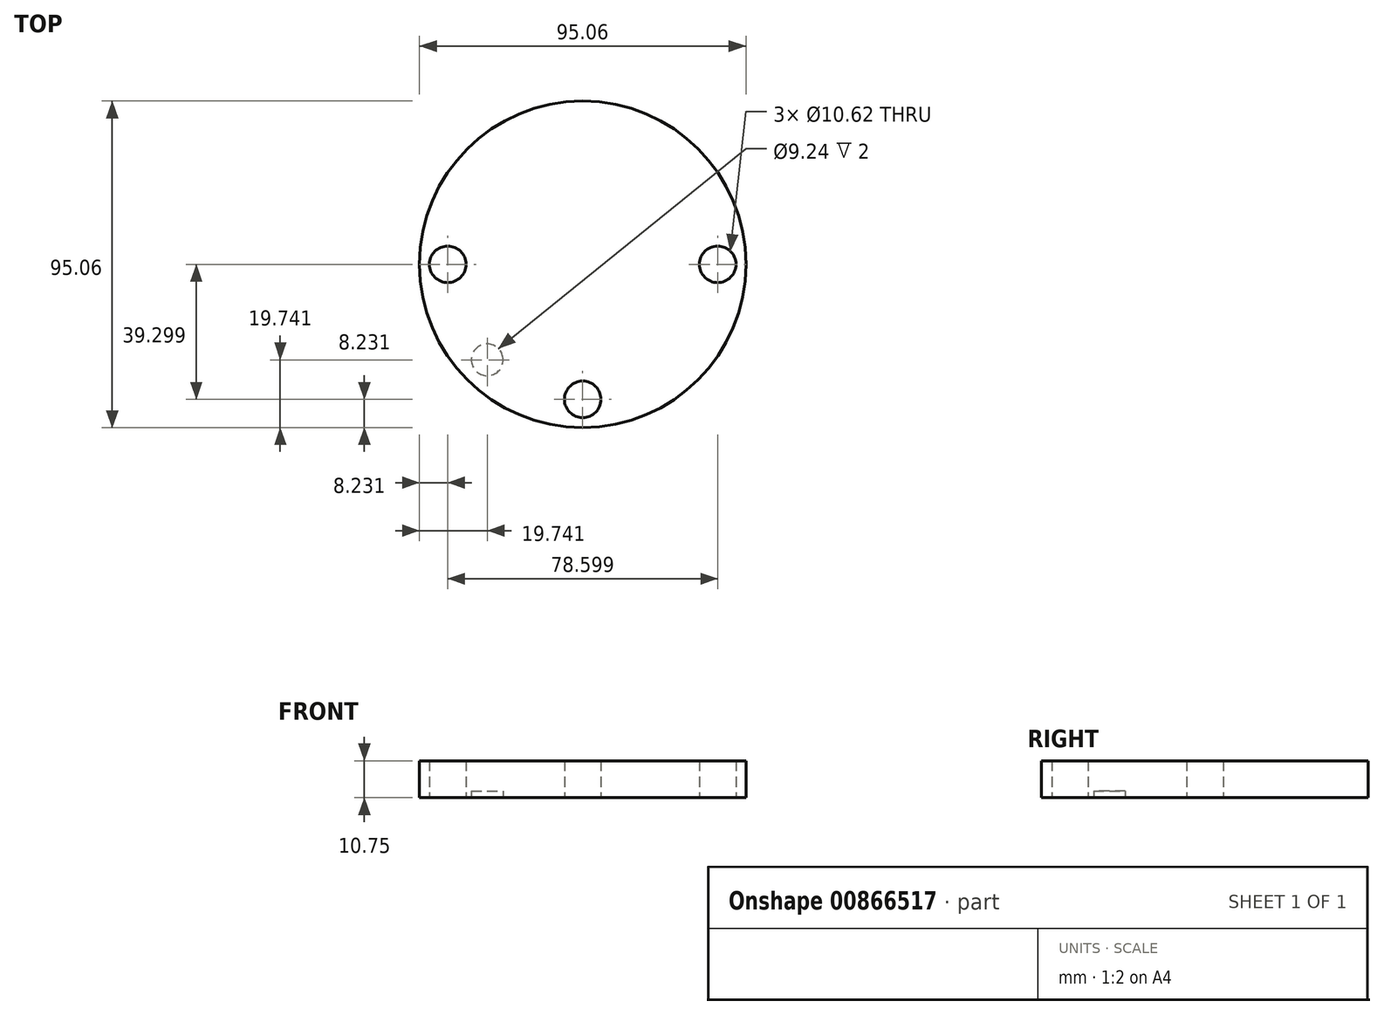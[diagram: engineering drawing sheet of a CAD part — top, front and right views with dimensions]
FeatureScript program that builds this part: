
annotation { "Feature Type Name" : "Feature", "Feature Type Description" : "" }
export const myFeature = defineFeature(function(context is Context, id is Id, definition is map)
    precondition{}
    {
        {
            var Q0;
            Q0=qCreatedBy(makeId("Front.planeOp"),FACE);
            var sketch = newSketch(context, id + "F0", { "sketchPlane" : qUnion([Q0])});
            skLineSegment(sketch, "E0", {"start": v(0, -21.77) * mm, "end": v(0, 44.18) * mm, "construction": true});
            skLineSegment(sketch, "E1", {"start": v(0, 0) * mm, "end": v(-47.53, 0) * mm});
            skLineSegment(sketch, "E2", {"start": v(-47.53, 0) * mm, "end": v(-47.53, -10.75) * mm});
            skLineSegment(sketch, "E3", {"start": v(-47.53, -10.75) * mm, "end": v(0, -10.75) * mm});
            skLineSegment(sketch, "E4", {"start": v(0, -10.75) * mm, "end": v(0, 0) * mm});
            skSolve(sketch);
        }
        {
            var Q0;
            Q0 = qSketchRegion(id + "F0", true);
            var Q1;
            Q1=sQuery(id+"F0.wireOp",EDGE,"E0");
            revolve(context, id + "F1", {"surfaceOperationType" : NewSurfaceOperationType.NEW, "entities" : qUnion([Q0]), "axis" : qUnion([Q1]), "revolveType" : RevolveType.FULL});
        }
        {
            var Q0;
            Q0=makeQuery(id+"F1.opRevolve","SWEPT_FACE",FACE,{"disambiguationData":[OSD([sQuery(id+"F0.wireOp",EDGE,"E3")])]});
            var sketch = newSketch(context, id + "F2", { "sketchPlane" : qUnion([Q0])});
            skLineSegment(sketch, "E5", {"start": v(0, 0) * mm, "end": v(0, 39.3) * mm, "construction": true});
            skLineSegment(sketch, "E6", {"start": v(0, 0) * mm, "end": v(-39.3, 0) * mm, "construction": true});
            skLineSegment(sketch, "E7", {"start": v(0, 0) * mm, "end": v(-27.79, 27.79) * mm, "construction": true});
            skCircle(sketch, "E8", {"center": v(0, 0) * mm, "radius": 39.3 * mm, "construction": true});
            skCircle(sketch, "E9", {"center": v(0, 39.3) * mm, "radius": 5.31 * mm});
            skCircle(sketch, "E10", {"center": v(-27.79, 27.79) * mm, "radius": 4.62 * mm});
            skCircle(sketch, "E11", {"center": v(-39.3, 0) * mm, "radius": 5.31 * mm});
            skCircle(sketch, "E12", {"center": v(39.3, 0) * mm, "radius": 5.31 * mm});
            skSolve(sketch);
        }
        {
            var Q0;
            Q0=makeQuery(id+"F2.imprint","IMPRINT",FACE,{"disambiguationData":[TD([[makeQuery(id+"F2.imprint","IMPRINT",EDGE,{"derivedFrom":sQuery(id+"F2.wireOp",EDGE,"E11")}),1.0]])]});
            var Q1;
            Q1=makeQuery(id+"F2.imprint","IMPRINT",FACE,{"disambiguationData":[TD([[makeQuery(id+"F2.imprint","IMPRINT",EDGE,{"derivedFrom":sQuery(id+"F2.wireOp",EDGE,"E9")}),1.0]])]});
            var Q2;
            Q2=makeQuery(id+"F2.imprint","IMPRINT",FACE,{"disambiguationData":[TD([[makeQuery(id+"F2.imprint","IMPRINT",EDGE,{"derivedFrom":sQuery(id+"F2.wireOp",EDGE,"E12")}),1.0]])]});
            extrude(context, id + "F3", {"entities" : qUnion([Q0, Q1, Q2]), "operationType" : NewBodyOperationType.REMOVE, "endBound" : BoundingType.THROUGH_ALL, "oppositeDirection" : true, "depth" : 25 * mm, "offsetDistance" : 25 * mm});
        }
        {
            var Q0;
            Q0=makeQuery(id+"F2.imprint","IMPRINT",FACE,{"disambiguationData":[TD([[makeQuery(id+"F2.imprint","IMPRINT",EDGE,{"derivedFrom":sQuery(id+"F2.wireOp",EDGE,"E10")}),1.0]])]});
            extrude(context, id + "F4", {"entities" : qUnion([Q0]), "operationType" : NewBodyOperationType.REMOVE, "oppositeDirection" : true, "depth" : 2 * mm, "offsetDistance" : 25 * mm});
        }
        {
            var Q0;
            Q0=makeQuery(id+"F1.opRevolve","SWEPT_FACE",FACE,{"disambiguationData":[OSD([sQuery(id+"F0.wireOp",EDGE,"E3")])]});
            var sketch = newSketch(context, id + "F5", { "sketchPlane" : qUnion([Q0])});
            skLineSegment(sketch, "E13", {"start": v(0, 0) * mm, "end": v(-27.79, 27.79) * mm, "construction": true});
            skSolve(sketch);
        }
    });
